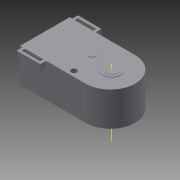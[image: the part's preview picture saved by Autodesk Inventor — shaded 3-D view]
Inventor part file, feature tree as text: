
AUTODESK INVENTOR PART (.ipt)
format: ipt  version: 2014 (Build 180170000, 170)  size: 178,176 bytes
history: native  units: mm
features: extrude x9, sketch x9, plane x1, fillet x1, mirror x1, other x1
ambient origin geometry x8: Origin, YZ Plane, XZ Plane, XY Plane, X Axis, Y Axis, Z Axis, Center Point
bodies: Volumenkörper1 (feature_tree)
feature tree (22):
  extrude  "Extrusion1"  Depth=20.0mm
  plane  "Arbeitsebene1"
  fillet  "Rundung1"  Radius=13.7mm
  extrude  "Extrusion2"  Depth=10.0mm
  extrude  "Extrusion4"  Depth=10.0mm
  extrude  "Extrusion8"  Depth=0.3mm TaperAngle=0.0deg
  extrude  "Extrusion5"  Depth=1.0mm
  extrude  "Extrusion9"  Depth=9.7mm TaperAngle=0.0deg
  extrude  "Extrusion10"  Depth=3.0mm
  extrude  "Extrusion11"  Depth=3.0mm
  extrude  "Extrusion12"  Depth=2.35mm TaperAngle=0.0deg
  mirror  "Spiegeln1"
  other  "Arbeitsachse1"
  sketch  "Skizze1"  dims[d0=36.5mm d1=20.0mm d2=13.7mm d3=0.0mm]
  sketch  "Skizze2"  dims[d4=10.0mm d5=5.0mm]
  sketch  "Skizze4"  dims[d6=10.0mm d7=12.0mm]
  sketch  "Skizze5"  dims[d8=3.0mm d9=0.3mm d10=0.0mm]
  sketch  "Skizze6"  dims[d15=2.3mm d16=1.0mm]
  sketch  "Skizze7"  dims[d17=18.5mm d18=9.7mm d19=0.0mm]
  sketch  "Skizze8"  dims[d21=3.0mm d23=5.0mm]
  sketch  "Skizze11"  dims[d24=9.5mm d27=3.0mm d28=6.6mm]
  sketch  "Skizze12"  dims[d29=16.1mm d30=9.7mm d31=0.0mm d34=7.3mm d37=0.53mm d38=0.0mm d40=3.0mm d42=10.1mm d43=19.2mm d44=0.2mm d45=0.0mm d46=0.3mm d47=0.0mm d49=9.5mm d50=2.8mm d51=1.0mm d52=2.35mm d53=0.0mm d54=1.0mm d55=1.0mm d56=1.0mm d57=2.35mm d58=0.0mm]
